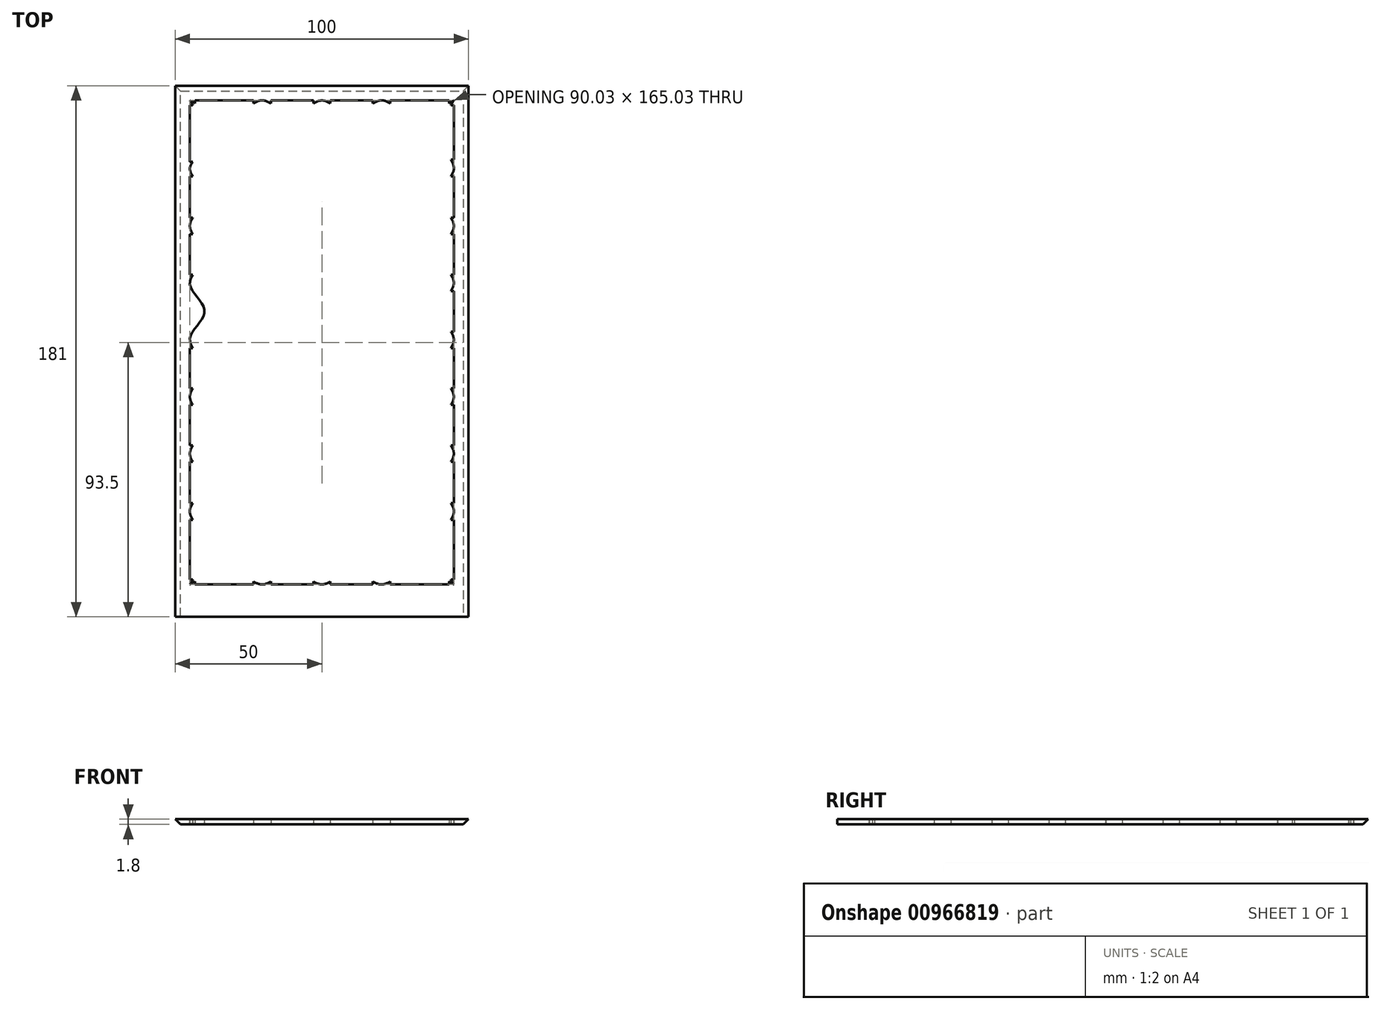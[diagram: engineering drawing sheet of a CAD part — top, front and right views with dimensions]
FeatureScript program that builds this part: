
annotation { "Feature Type Name" : "Feature", "Feature Type Description" : "" }
export const myFeature = defineFeature(function(context is Context, id is Id, definition is map)
    precondition{}
    {
        {
            var Q0;
            Q0=qCreatedBy(makeId("Top.planeOp"),FACE);
            var sketch = newSketch(context, id + "F0", { "sketchPlane" : qUnion([Q0])});
            skLineSegment(sketch, "E0.bottom", {"start": v(-50, 90) * mm, "end": v(50, 90) * mm});
            skLineSegment(sketch, "E0.left", {"start": v(-50, 90) * mm, "end": v(-50, -90) * mm});
            skLineSegment(sketch, "E0.right", {"start": v(50, 90) * mm, "end": v(50, -90) * mm});
            skLineSegment(sketch, "E1.bottom", {"start": v(-43.3, 85) * mm, "end": v(-23.33, 85) * mm});
            skLineSegment(sketch, "E1.top", {"start": v(-43.3, -80) * mm, "end": v(-23.33, -80) * mm});
            skLineSegment(sketch, "E1.left", {"start": v(-45, 83.32) * mm, "end": v(-45, 64.07) * mm});
            skLineSegment(sketch, "E1.right", {"start": v(45, 83.36) * mm, "end": v(45, 64.83) * mm});
            skFitSpline(sketch, "E2", {"points": [v(-45, 85) * mm, v(-30, 80) * mm, v(-20, 85) * mm, v(-10, 80) * mm, v(0, 85) * mm, v(10, 80) * mm, v(20, 85) * mm, v(30, 80) * mm, v(45, 85) * mm], "startDerivative": vector(112.01, -66.4) * mm, "endDerivative": vector(112.01, 66.4) * mm});
            skLineSegment(sketch, "E3", {"start": v(-45, 6.18) * mm, "end": v(-45, 20.01) * mm, "construction": true});
            skFitSpline(sketch, "E4", {"points": [v(-45, 85) * mm, v(-40, 69.3) * mm, v(-45, 61.6) * mm, v(-40, 51.9) * mm, v(-45, 42.2) * mm, v(-40, 32.5) * mm, v(-45, 22.8) * mm, v(-40, 13.1) * mm, v(-45, 3.4) * mm, v(-40, -6.3) * mm, v(-45, -16) * mm, v(-40, -25.7) * mm, v(-45, -35.4) * mm, v(-40, -45.1) * mm, v(-45, -54.8) * mm, v(-40, -64.4) * mm, v(-45, -80) * mm], "startDerivative": vector(129.63, -214.28) * mm, "endDerivative": vector(-130, -213.67) * mm});
            skFitSpline(sketch, "E5", {"points": [v(-5.54, 50.63) * mm, v(-5.28, 46.28) * mm, v(-7.2, 42.58) * mm, v(-10.84, 40.44) * mm]});
            skFitSpline(sketch, "E6", {"points": [v(-10.84, 40.44) * mm, v(-11.43, 40.1) * mm, v(-11.89, 39.92) * mm, v(-13.41, 39.47) * mm]});
            skFitSpline(sketch, "E7", {"points": [v(-13.41, 39.47) * mm, v(-14.56, 39.14) * mm, v(-15.58, 38.9) * mm, v(-16.1, 38.83) * mm]});
            skFitSpline(sketch, "E8", {"points": [v(-16.1, 38.83) * mm, v(-21.18, 38.21) * mm, v(-24.88, 40.32) * mm, v(-27.01, 45.08) * mm]});
            skFitSpline(sketch, "E9", {"points": [v(-27.01, 45.08) * mm, v(-27.53, 46.22) * mm, v(-28.4, 49.5) * mm, v(-28.56, 50.86) * mm]});
            skFitSpline(sketch, "E10", {"points": [v(-28.56, 50.86) * mm, v(-29.19, 56.39) * mm, v(-27.84, 62.48) * mm, v(-25.25, 65.85) * mm]});
            skFitSpline(sketch, "E11", {"points": [v(-25.25, 65.85) * mm, v(-24.94, 66.25) * mm, v(-24.35, 66.87) * mm, v(-23.93, 67.23) * mm]});
            skFitSpline(sketch, "E12", {"points": [v(-23.93, 67.23) * mm, v(-23.2, 67.86) * mm, v(-23.13, 67.9) * mm, v(-22.09, 68.2) * mm]});
            skFitSpline(sketch, "E13", {"points": [v(-22.09, 68.2) * mm, v(-21.14, 68.5) * mm, v(-20.9, 68.53) * mm, v(-20.15, 68.5) * mm]});
            skFitSpline(sketch, "E14", {"points": [v(-20.15, 68.5) * mm, v(-15.63, 68.31) * mm, v(-9.95, 63.07) * mm, v(-7.09, 56.44) * mm]});
            skFitSpline(sketch, "E15", {"points": [v(-7.09, 56.44) * mm, v(-6.38, 54.8) * mm, v(-5.62, 51.95) * mm, v(-5.54, 50.63) * mm]});
            skLineSegment(sketch, "E16.0", {"start": v(-14.32, 39.23) * mm, "end": v(-13.41, 39.47) * mm, "construction": true});
            skLineSegment(sketch, "E16.1", {"start": v(-14.32, 39.23) * mm, "end": v(-22.09, 68.2) * mm, "construction": true});
            skFitSpline(sketch, "E17", {"points": [v(30.12, 27.9) * mm, v(27.84, 24.19) * mm, v(24.14, 22.26) * mm, v(19.94, 22.6) * mm]});
            skFitSpline(sketch, "E18", {"points": [v(19.94, 22.6) * mm, v(19.26, 22.65) * mm, v(18.78, 22.77) * mm, v(17.28, 23.27) * mm]});
            skFitSpline(sketch, "E19", {"points": [v(17.28, 23.27) * mm, v(16.14, 23.66) * mm, v(15.16, 24.04) * mm, v(14.71, 24.28) * mm]});
            skFitSpline(sketch, "E20", {"points": [v(14.71, 24.28) * mm, v(10.19, 26.7) * mm, v(8.37, 30.54) * mm, v(9.35, 35.67) * mm]});
            skFitSpline(sketch, "E21", {"points": [v(9.35, 35.67) * mm, v(9.58, 36.9) * mm, v(10.75, 40.08) * mm, v(11.4, 41.3) * mm]});
            skFitSpline(sketch, "E22", {"points": [v(11.4, 41.3) * mm, v(14.05, 46.18) * mm, v(18.65, 50.4) * mm, v(22.71, 51.67) * mm]});
            skFitSpline(sketch, "E23", {"points": [v(22.71, 51.67) * mm, v(23.2, 51.82) * mm, v(24.04, 51.99) * mm, v(24.58, 52.04) * mm]});
            skFitSpline(sketch, "E24", {"points": [v(24.58, 52.04) * mm, v(25.54, 52.14) * mm, v(25.61, 52.13) * mm, v(26.65, 51.79) * mm]});
            skFitSpline(sketch, "E25", {"points": [v(26.65, 51.79) * mm, v(27.6, 51.48) * mm, v(27.8, 51.37) * mm, v(28.4, 50.91) * mm]});
            skFitSpline(sketch, "E26", {"points": [v(28.4, 50.91) * mm, v(32, 48.17) * mm, v(33.65, 40.62) * mm, v(32.19, 33.54) * mm]});
            skFitSpline(sketch, "E27", {"points": [v(32.19, 33.54) * mm, v(31.83, 31.79) * mm, v(30.82, 29.02) * mm, v(30.12, 27.9) * mm]});
            skLineSegment(sketch, "E28.0", {"start": v(16.39, 23.6) * mm, "end": v(17.28, 23.27) * mm, "construction": true});
            skLineSegment(sketch, "E28.1", {"start": v(16.39, 23.6) * mm, "end": v(26.65, 51.79) * mm, "construction": true});
            skFitSpline(sketch, "E29", {"points": [v(-1.78, 4.85) * mm, v(-0.6, 0.66) * mm, v(-1.71, -3.36) * mm, v(-4.81, -6.22) * mm]});
            skFitSpline(sketch, "E30", {"points": [v(-4.81, -6.22) * mm, v(-5.32, -6.69) * mm, v(-5.73, -6.95) * mm, v(-7.12, -7.7) * mm]});
            skFitSpline(sketch, "E31", {"points": [v(-7.12, -7.7) * mm, v(-8.17, -8.28) * mm, v(-9.12, -8.74) * mm, v(-9.6, -8.9) * mm]});
            skFitSpline(sketch, "E32", {"points": [v(-9.6, -8.9) * mm, v(-14.45, -10.58) * mm, v(-18.5, -9.3) * mm, v(-21.6, -5.1) * mm]});
            skFitSpline(sketch, "E33", {"points": [v(-21.6, -5.1) * mm, v(-22.34, -4.1) * mm, v(-23.9, -1.07) * mm, v(-24.33, 0.23) * mm]});
            skFitSpline(sketch, "E34", {"points": [v(-24.33, 0.23) * mm, v(-26.11, 5.5) * mm, v(-26.08, 11.74) * mm, v(-24.26, 15.58) * mm]});
            skFitSpline(sketch, "E35", {"points": [v(-24.26, 15.58) * mm, v(-24.04, 16.03) * mm, v(-23.6, 16.77) * mm, v(-23.26, 17.2) * mm]});
            skFitSpline(sketch, "E36", {"points": [v(-23.26, 17.2) * mm, v(-22.67, 17.97) * mm, v(-22.62, 18.02) * mm, v(-21.67, 18.55) * mm]});
            skFitSpline(sketch, "E37", {"points": [v(-21.67, 18.55) * mm, v(-20.8, 19.03) * mm, v(-20.58, 19.11) * mm, v(-19.83, 19.24) * mm]});
            skFitSpline(sketch, "E38", {"points": [v(-19.83, 19.24) * mm, v(-15.37, 20.01) * mm, v(-8.72, 16.09) * mm, v(-4.52, 10.2) * mm]});
            skFitSpline(sketch, "E39", {"points": [v(-4.52, 10.2) * mm, v(-3.48, 8.75) * mm, v(-2.13, 6.13) * mm, v(-1.78, 4.85) * mm]});
            skLineSegment(sketch, "E40.0", {"start": v(-7.96, -8.14) * mm, "end": v(-7.12, -7.7) * mm, "construction": true});
            skLineSegment(sketch, "E40.1", {"start": v(-7.96, -8.14) * mm, "end": v(-21.67, 18.55) * mm, "construction": true});
            skFitSpline(sketch, "E41", {"points": [v(25.15, -37.2) * mm, v(22.55, -40.7) * mm, v(18.7, -42.3) * mm, v(14.54, -41.6) * mm]});
            skFitSpline(sketch, "E42", {"points": [v(14.54, -41.6) * mm, v(13.86, -41.49) * mm, v(13.4, -41.32) * mm, v(11.95, -40.69) * mm]});
            skFitSpline(sketch, "E43", {"points": [v(11.95, -40.69) * mm, v(10.85, -40.2) * mm, v(9.9, -39.74) * mm, v(9.48, -39.46) * mm]});
            skFitSpline(sketch, "E44", {"points": [v(9.48, -39.46) * mm, v(5.18, -36.66) * mm, v(3.71, -32.67) * mm, v(5.13, -27.65) * mm]});
            skFitSpline(sketch, "E45", {"points": [v(5.13, -27.65) * mm, v(5.47, -26.45) * mm, v(6.9, -23.37) * mm, v(7.67, -22.23) * mm]});
            skFitSpline(sketch, "E46", {"points": [v(7.67, -22.23) * mm, v(10.73, -17.59) * mm, v(15.68, -13.78) * mm, v(19.84, -12.87) * mm]});
            skFitSpline(sketch, "E47", {"points": [v(19.84, -12.87) * mm, v(20.33, -12.76) * mm, v(21.18, -12.67) * mm, v(21.73, -12.66) * mm]});
            skFitSpline(sketch, "E48", {"points": [v(21.73, -12.66) * mm, v(22.7, -12.65) * mm, v(22.77, -12.67) * mm, v(23.77, -13.1) * mm]});
            skFitSpline(sketch, "E49", {"points": [v(23.77, -13.1) * mm, v(24.69, -13.5) * mm, v(24.89, -13.61) * mm, v(25.45, -14.12) * mm]});
            skFitSpline(sketch, "E50", {"points": [v(25.45, -14.12) * mm, v(28.79, -17.17) * mm, v(29.77, -24.83) * mm, v(27.7, -31.76) * mm]});
            skFitSpline(sketch, "E51", {"points": [v(27.7, -31.76) * mm, v(27.19, -33.47) * mm, v(25.94, -36.14) * mm, v(25.15, -37.2) * mm]});
            skLineSegment(sketch, "E52.0", {"start": v(11.1, -40.29) * mm, "end": v(11.95, -40.69) * mm, "construction": true});
            skLineSegment(sketch, "E52.1", {"start": v(11.1, -40.29) * mm, "end": v(23.77, -13.1) * mm, "construction": true});
            skFitSpline(sketch, "E53", {"points": [v(-3.82, -48.4) * mm, v(-2.09, -52.4) * mm, v(-2.63, -56.53) * mm, v(-5.32, -59.79) * mm]});
            skFitSpline(sketch, "E54", {"points": [v(-5.32, -59.79) * mm, v(-5.75, -60.32) * mm, v(-6.12, -60.63) * mm, v(-7.4, -61.58) * mm]});
            skFitSpline(sketch, "E55", {"points": [v(-7.4, -61.58) * mm, v(-8.36, -62.28) * mm, v(-9.24, -62.87) * mm, v(-9.7, -63.1) * mm]});
            skFitSpline(sketch, "E56", {"points": [v(-9.7, -63.1) * mm, v(-14.27, -65.42) * mm, v(-18.46, -64.7) * mm, v(-22.1, -60.96) * mm]});
            skFitSpline(sketch, "E57", {"points": [v(-22.1, -60.96) * mm, v(-22.97, -60.07) * mm, v(-24.92, -57.28) * mm, v(-25.53, -56.06) * mm]});
            skFitSpline(sketch, "E58", {"points": [v(-25.53, -56.06) * mm, v(-28.01, -51.08) * mm, v(-28.83, -44.9) * mm, v(-27.54, -40.84) * mm]});
            skFitSpline(sketch, "E59", {"points": [v(-27.54, -40.84) * mm, v(-27.4, -40.36) * mm, v(-27.05, -39.57) * mm, v(-26.78, -39.1) * mm]});
            skFitSpline(sketch, "E60", {"points": [v(-26.78, -39.1) * mm, v(-26.3, -38.25) * mm, v(-26.26, -38.2) * mm, v(-25.38, -37.54) * mm]});
            skFitSpline(sketch, "E61", {"points": [v(-25.38, -37.54) * mm, v(-24.58, -36.95) * mm, v(-24.38, -36.83) * mm, v(-23.65, -36.6) * mm]});
            skFitSpline(sketch, "E62", {"points": [v(-23.65, -36.6) * mm, v(-19.35, -35.24) * mm, v(-12.22, -38.22) * mm, v(-7.26, -43.47) * mm]});
            skFitSpline(sketch, "E63", {"points": [v(-7.26, -43.47) * mm, v(-6.03, -44.77) * mm, v(-4.34, -47.2) * mm, v(-3.82, -48.4) * mm]});
            skLineSegment(sketch, "E64.0", {"start": v(-8.17, -62.12) * mm, "end": v(-7.4, -61.58) * mm, "construction": true});
            skLineSegment(sketch, "E64.1", {"start": v(-8.17, -62.12) * mm, "end": v(-25.38, -37.54) * mm, "construction": true});
            skFitSpline(sketch, "E65.trimOffspring", {"points": [v(-45, 85) * mm, v(-40, 69.3) * mm, v(-45, 61.6) * mm, v(-40, 51.9) * mm, v(-45, 42.2) * mm, v(-40, 32.5) * mm, v(-45, 22.8) * mm, v(-40, 13.1) * mm, v(-45, 3.4) * mm, v(-40, -6.3) * mm, v(-45, -16) * mm, v(-40, -25.7) * mm, v(-45, -35.4) * mm, v(-40, -45.1) * mm, v(-45, -54.8) * mm, v(-40, -64.4) * mm, v(-45, -80) * mm], "startDerivative": vector(129.63, -214.28) * mm, "endDerivative": vector(-130, -213.67) * mm});
            skFitSpline(sketch, "E66.trimOffspring", {"points": [v(-45, -80) * mm, v(-30, -75) * mm, v(-20, -80) * mm, v(-10, -75) * mm, v(0, -80) * mm, v(10, -75) * mm, v(20, -80) * mm, v(30, -75) * mm, v(45, -80) * mm], "startDerivative": vector(112.01, 66.4) * mm, "endDerivative": vector(112.01, -66.4) * mm});
            skFitSpline(sketch, "E67.trimOffspring", {"points": [v(45, 85) * mm, v(40, 71.3) * mm, v(45, 61.6) * mm, v(40, 51.9) * mm, v(45, 42.2) * mm, v(40, 32.5) * mm, v(45, 22.8) * mm, v(40, 13.1) * mm, v(45, 3.4) * mm, v(40, -6.3) * mm, v(45, -16) * mm, v(40, -25.7) * mm, v(45, -35.4) * mm, v(40, -45.1) * mm, v(45, -54.8) * mm, v(40, -64.4) * mm, v(45, -80) * mm], "startDerivative": vector(-129.63, -214.28) * mm, "endDerivative": vector(130, -213.67) * mm});
            skLineSegment(sketch, "E68.trimOffspring", {"start": v(45, -16) * mm, "end": v(45, -16) * mm});
            skLineSegment(sketch, "E69.trimOffspring", {"start": v(45, 3.4) * mm, "end": v(45, 3.4) * mm});
            skLineSegment(sketch, "E70.trimOffspring", {"start": v(45, 22.8) * mm, "end": v(45, 22.8) * mm});
            skLineSegment(sketch, "E71", {"start": v(-44, 83.32) * mm, "end": v(-45, 83.32) * mm});
            skLineSegment(sketch, "E72", {"start": v(-43.3, 84) * mm, "end": v(-43.3, 85) * mm});
            skLineSegment(sketch, "E73", {"start": v(-23.33, 84) * mm, "end": v(-23.33, 85) * mm});
            skLineSegment(sketch, "E74", {"start": v(-17.4, 84) * mm, "end": v(-17.4, 85) * mm});
            skLineSegment(sketch, "E75", {"start": v(-2.88, 84) * mm, "end": v(-2.88, 85) * mm});
            skLineSegment(sketch, "E76", {"start": v(2.88, 84) * mm, "end": v(2.88, 85) * mm});
            skLineSegment(sketch, "E77", {"start": v(17.4, 84) * mm, "end": v(17.4, 85) * mm});
            skLineSegment(sketch, "E78", {"start": v(23.33, 84) * mm, "end": v(23.33, 85) * mm});
            skLineSegment(sketch, "E79", {"start": v(43.3, 84) * mm, "end": v(43.3, 85) * mm});
            skLineSegment(sketch, "E80", {"start": v(44, 83.36) * mm, "end": v(45, 83.36) * mm});
            skLineSegment(sketch, "E81", {"start": v(44, 64.83) * mm, "end": v(45, 64.83) * mm});
            skLineSegment(sketch, "E82", {"start": v(44, 59.05) * mm, "end": v(45, 59.05) * mm});
            skLineSegment(sketch, "E83", {"start": v(44, 45.01) * mm, "end": v(45, 45.01) * mm});
            skLineSegment(sketch, "E84", {"start": v(44, 39.43) * mm, "end": v(45, 39.43) * mm});
            skLineSegment(sketch, "E85", {"start": v(44, 25.58) * mm, "end": v(45, 25.58) * mm});
            skLineSegment(sketch, "E86", {"start": v(44, 20.01) * mm, "end": v(45, 20.01) * mm});
            skLineSegment(sketch, "E87", {"start": v(44, 6.18) * mm, "end": v(45, 6.18) * mm});
            skLineSegment(sketch, "E88", {"start": v(44, 0.61) * mm, "end": v(45, 0.61) * mm});
            skLineSegment(sketch, "E89", {"start": v(44, -18.8) * mm, "end": v(45, -18.8) * mm});
            skLineSegment(sketch, "E90", {"start": v(44, -13.22) * mm, "end": v(45, -13.22) * mm});
            skLineSegment(sketch, "E91", {"start": v(44, -32.64) * mm, "end": v(45, -32.64) * mm});
            skLineSegment(sketch, "E92", {"start": v(44, -38.22) * mm, "end": v(45, -38.22) * mm});
            skLineSegment(sketch, "E93", {"start": v(44, -52.3) * mm, "end": v(45, -52.3) * mm});
            skLineSegment(sketch, "E94", {"start": v(44, -58) * mm, "end": v(45, -58) * mm});
            skLineSegment(sketch, "E95", {"start": v(43.3, -79) * mm, "end": v(43.3, -80) * mm});
            skLineSegment(sketch, "E96", {"start": v(44, -78.33) * mm, "end": v(45, -78.33) * mm});
            skLineSegment(sketch, "E97", {"start": v(23.33, -79) * mm, "end": v(23.33, -80) * mm});
            skLineSegment(sketch, "E98", {"start": v(17.4, -79) * mm, "end": v(17.4, -80) * mm});
            skLineSegment(sketch, "E99", {"start": v(2.88, -79) * mm, "end": v(2.88, -80) * mm});
            skLineSegment(sketch, "E100", {"start": v(2.88, -80) * mm, "end": v(2.87, -79.93) * mm});
            skLineSegment(sketch, "E101", {"start": v(-2.88, -79) * mm, "end": v(-2.88, -80) * mm});
            skLineSegment(sketch, "E102", {"start": v(-17.4, -79) * mm, "end": v(-17.4, -80) * mm});
            skLineSegment(sketch, "E103", {"start": v(-23.33, -79) * mm, "end": v(-23.33, -80) * mm});
            skLineSegment(sketch, "E104", {"start": v(-43.3, -79) * mm, "end": v(-43.3, -80) * mm});
            skLineSegment(sketch, "E105", {"start": v(-44, -78.33) * mm, "end": v(-45, -78.33) * mm});
            skLineSegment(sketch, "E106", {"start": v(-44, -58) * mm, "end": v(-45, -58) * mm});
            skLineSegment(sketch, "E107", {"start": v(-44, -52.3) * mm, "end": v(-45, -52.3) * mm});
            skLineSegment(sketch, "E108", {"start": v(-44, -38.22) * mm, "end": v(-45, -38.22) * mm});
            skLineSegment(sketch, "E109", {"start": v(-44, -32.64) * mm, "end": v(-45, -32.64) * mm});
            skLineSegment(sketch, "E110", {"start": v(-44, -18.8) * mm, "end": v(-45, -18.8) * mm});
            skLineSegment(sketch, "E111", {"start": v(-44, -13.22) * mm, "end": v(-45, -13.22) * mm});
            skLineSegment(sketch, "E112", {"start": v(-44, 0.61) * mm, "end": v(-45, 0.61) * mm});
            skLineSegment(sketch, "E113", {"start": v(-44, 6.18) * mm, "end": v(-45, 6.18) * mm});
            skLineSegment(sketch, "E114", {"start": v(-44, 20.01) * mm, "end": v(-45, 20.01) * mm});
            skLineSegment(sketch, "E115", {"start": v(-44, 25.58) * mm, "end": v(-45, 25.58) * mm});
            skLineSegment(sketch, "E116", {"start": v(-44, 39.43) * mm, "end": v(-45, 39.43) * mm});
            skLineSegment(sketch, "E117", {"start": v(-44, 44.96) * mm, "end": v(-45, 44.96) * mm});
            skLineSegment(sketch, "E118", {"start": v(-44, 59.1) * mm, "end": v(-45, 59.1) * mm});
            skLineSegment(sketch, "E119", {"start": v(-44, 64.07) * mm, "end": v(-45, 64.07) * mm});
            skLineSegment(sketch, "E120.trimOffspring", {"start": v(-17.4, 85) * mm, "end": v(-2.88, 85) * mm});
            skLineSegment(sketch, "E121.trimOffspring", {"start": v(2.88, 85) * mm, "end": v(17.4, 85) * mm});
            skLineSegment(sketch, "E122.trimOffspring", {"start": v(23.33, 85) * mm, "end": v(43.3, 85) * mm});
            skLineSegment(sketch, "E123.trimOffspring", {"start": v(-45, 59.1) * mm, "end": v(-45, 44.96) * mm});
            skLineSegment(sketch, "E124.trimOffspring", {"start": v(-45, 39.43) * mm, "end": v(-45, 25.58) * mm});
            skLineSegment(sketch, "E125.trimOffspring", {"start": v(-45, 20.01) * mm, "end": v(-45, 6.18) * mm});
            skLineSegment(sketch, "E126.trimOffspring", {"start": v(-45, 0.61) * mm, "end": v(-45, -13.22) * mm});
            skLineSegment(sketch, "E127.trimOffspring", {"start": v(-45, -18.8) * mm, "end": v(-45, -32.64) * mm});
            skLineSegment(sketch, "E128.trimOffspring", {"start": v(-45, -38.22) * mm, "end": v(-45, -52.3) * mm});
            skLineSegment(sketch, "E129.trimOffspring", {"start": v(-45, -58) * mm, "end": v(-45, -78.33) * mm});
            skLineSegment(sketch, "E130.trimOffspring", {"start": v(-17.4, -80) * mm, "end": v(-2.88, -80) * mm});
            skLineSegment(sketch, "E131.trimOffspring", {"start": v(2.88, -80) * mm, "end": v(17.4, -80) * mm});
            skLineSegment(sketch, "E132.trimOffspring", {"start": v(23.33, -80) * mm, "end": v(43.3, -80) * mm});
            skLineSegment(sketch, "E133.trimOffspring", {"start": v(45, -58) * mm, "end": v(45, -78.33) * mm});
            skLineSegment(sketch, "E134.trimOffspring", {"start": v(45, -38.22) * mm, "end": v(45, -52.3) * mm});
            skLineSegment(sketch, "E135.trimOffspring", {"start": v(45, -18.8) * mm, "end": v(45, -32.64) * mm});
            skLineSegment(sketch, "E136.trimOffspring", {"start": v(45, 0.61) * mm, "end": v(45, -13.22) * mm});
            skLineSegment(sketch, "E137.trimOffspring", {"start": v(45, 20.01) * mm, "end": v(45, 6.18) * mm});
            skLineSegment(sketch, "E138.trimOffspring", {"start": v(45, 39.43) * mm, "end": v(45, 25.58) * mm});
            skLineSegment(sketch, "E139.trimOffspring", {"start": v(45, 59.05) * mm, "end": v(45, 45.01) * mm});
            skLineSegment(sketch, "E140.top", {"start": v(-50, -91) * mm, "end": v(50, -91) * mm});
            skLineSegment(sketch, "E140.left", {"start": v(-50, -90) * mm, "end": v(-50, -91) * mm});
            skLineSegment(sketch, "E140.right", {"start": v(50, -90) * mm, "end": v(50, -91) * mm});
            skSolve(sketch);
        }
        {
            var Q0;
            Q0 = qSketchRegion(id + "F0", true);
            extrude(context, id + "F1", {"entities" : qUnion([Q0]), "depth" : 1.8 * mm, "offsetDistance" : 25 * mm});
        }
        {
            var Q0;
            Q0=makeQuery(id+"F1.opExtrude","CAP_EDGE",EDGE,{"disambiguationData":[OSD([sQuery(id+"F0.wireOp",EDGE,"E0.bottom")])],"isStart":true});
            var Q1;
            Q1=makeQuery(id+"F1.opExtrude","CAP_EDGE",EDGE,{"disambiguationData":[OSD([sQuery(id+"F0.wireOp",EDGE,"E0.left")])],"isStart":true});
            var Q2;
            Q2=makeQuery(id+"F1.opExtrude","CAP_EDGE",EDGE,{"disambiguationData":[OSD([sQuery(id+"F0.wireOp",EDGE,"E0.right")])],"isStart":true});
            chamfer(context, id + "F2", {"entities" : qUnion([Q0, Q1, Q2]), "width" : 1.8 * mm, "tangentPropagation" : true});
        }
    });
